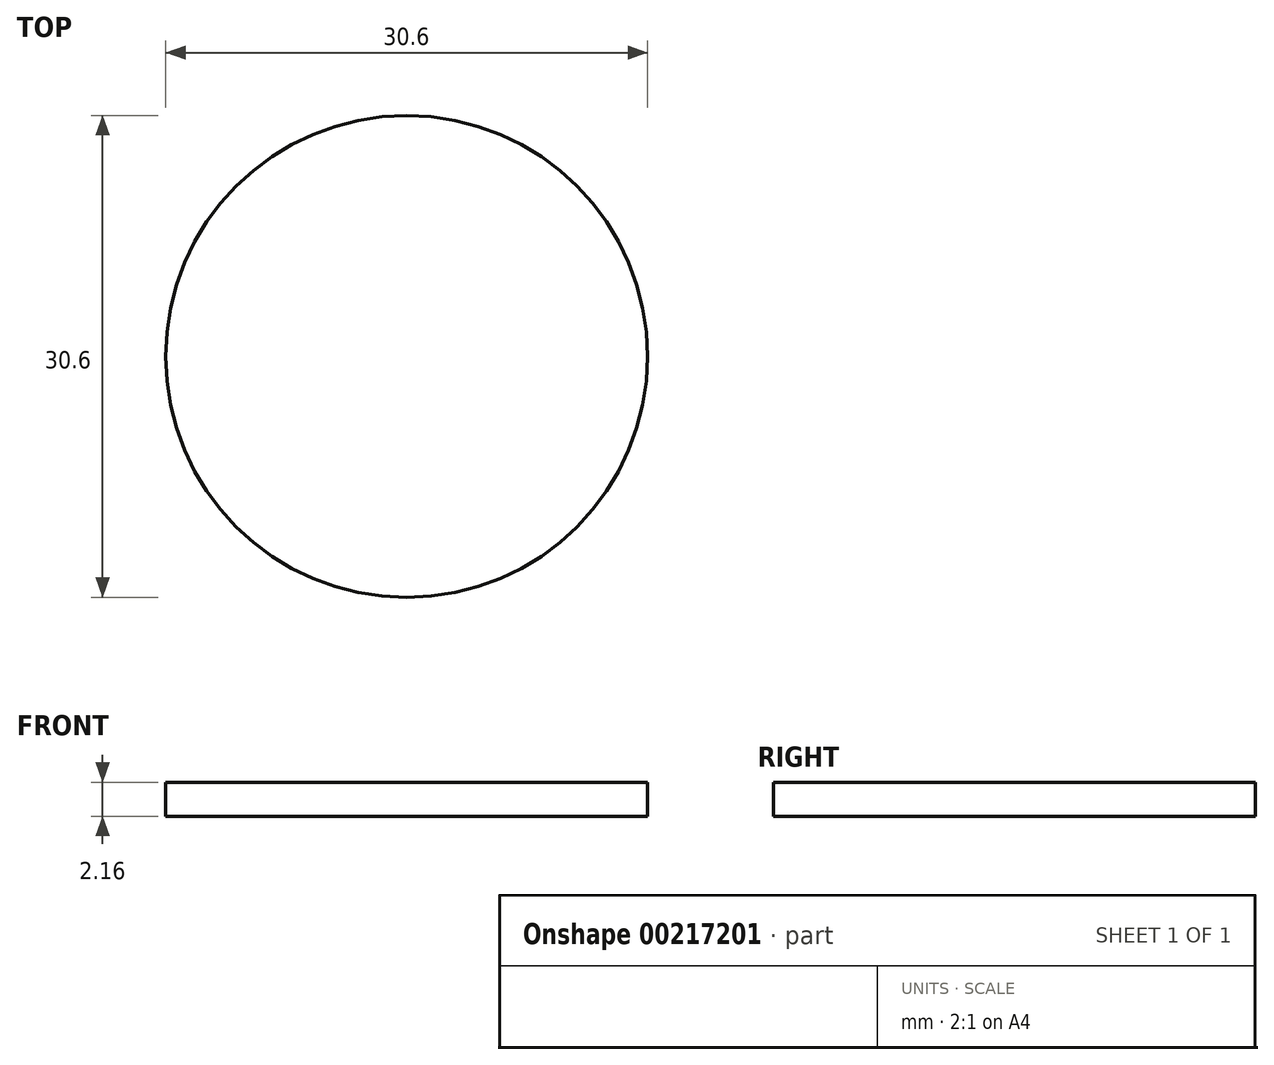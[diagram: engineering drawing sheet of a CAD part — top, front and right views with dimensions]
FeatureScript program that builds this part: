
annotation { "Feature Type Name" : "Feature", "Feature Type Description" : "" }
export const myFeature = defineFeature(function(context is Context, id is Id, definition is map)
    precondition{}
    {
        {
            var Q0;
            Q0=qCreatedBy(makeId("Top.planeOp"),FACE);
            var sketch = newSketch(context, id + "F0", { "sketchPlane" : qUnion([Q0])});
            skCircle(sketch, "E0", {"center": v(0, 0) * mm, "radius": 15.3 * mm});
            skSolve(sketch);
        }
        {
            var Q0;
            Q0=qSketchRegion(id+"F0",true);
            extrude(context, id + "F1", {"entities" : qUnion([Q0]), "endBound" : BoundingType.SYMMETRIC, "depth" : 2.15 * mm});
        }
    });
